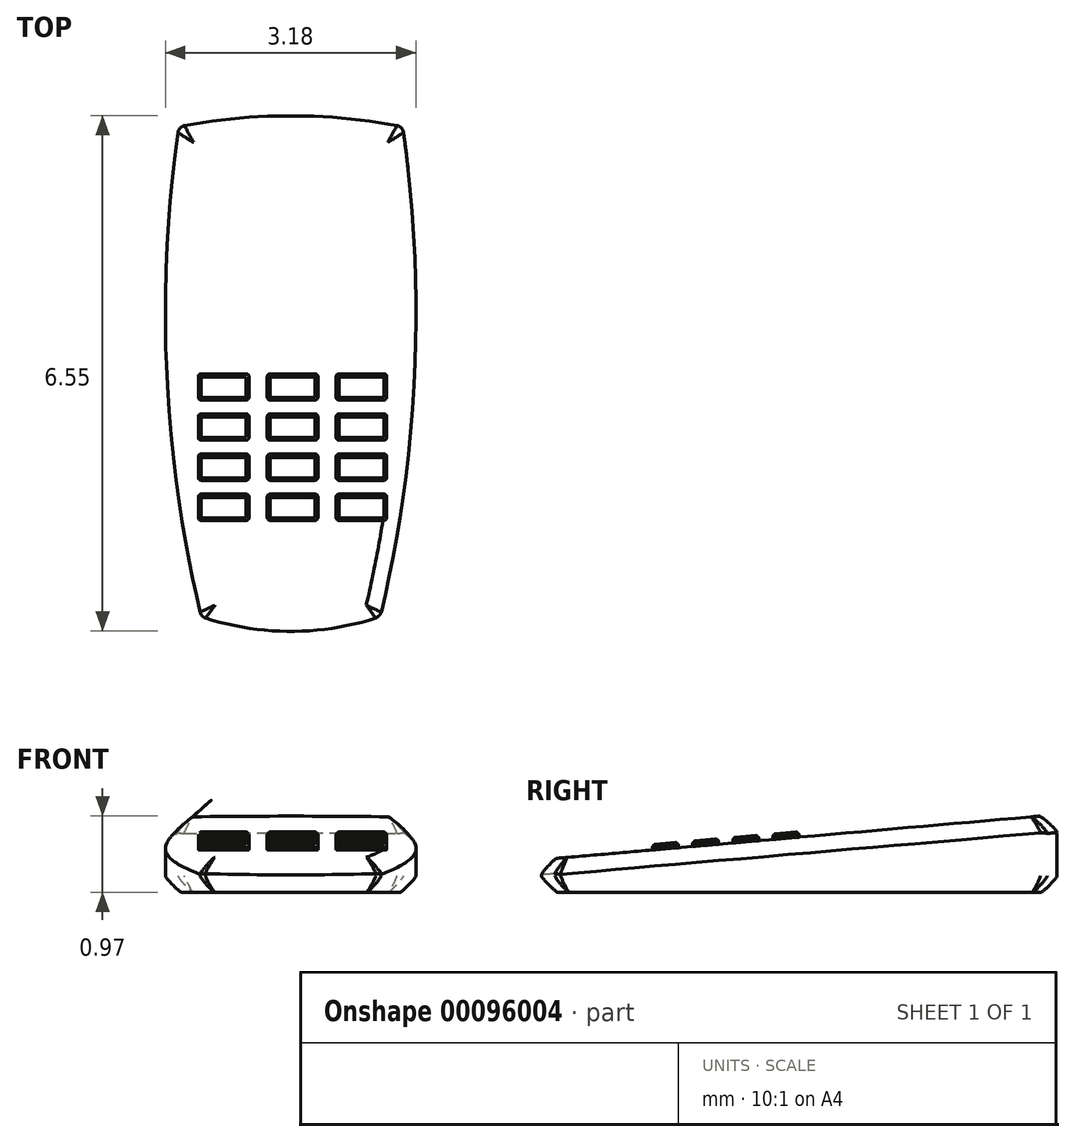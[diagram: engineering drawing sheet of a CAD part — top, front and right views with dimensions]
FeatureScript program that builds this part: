
annotation { "Feature Type Name" : "Feature", "Feature Type Description" : "" }
export const myFeature = defineFeature(function(context is Context, id is Id, definition is map)
    precondition{}
    {
        {
            var Q0;
            Q0=qCreatedBy(makeId("Top.planeOp"),FACE);
            var sketch = newSketch(context, id + "F0", { "sketchPlane" : qUnion([Q0])});
            skPoint(sketch, "E0", {"position": v(-40.64, 114.48) * mm});
            skPoint(sketch, "E1", {"position": v(-32.5, -63.32) * mm});
            skPoint(sketch, "E2.MirrorP", {"position": v(40.64, 114.48) * mm});
            skPoint(sketch, "E3.MirrorP", {"position": v(32.5, -63.32) * mm});
            skArc(sketch, "E4", {"start": v(38.52, 114.88) * mm, "mid": v(0, 118.42) * mm, "end": v(-38.52, 114.88) * mm});
            skArc(sketch, "E5", {"start": v(-40.94, 112.35) * mm, "mid": v(-45, 24.95) * mm, "end": v(-32.89, -61.7) * mm});
            skArc(sketch, "E6", {"start": v(-30.9, -63.86) * mm, "mid": v(0, -68.73) * mm, "end": v(30.9, -63.86) * mm});
            skArc(sketch, "E7.MirrorCS", {"start": v(40.94, 112.35) * mm, "mid": v(45, 24.95) * mm, "end": v(32.89, -61.7) * mm});
            skArc(sketch, "E8.filletArc", {"start": v(-38.52, 114.88) * mm, "mid": v(-40.14, 114) * mm, "end": v(-40.94, 112.35) * mm});
            skArc(sketch, "E9.filletArc", {"start": v(40.94, 112.35) * mm, "mid": v(40.14, 114) * mm, "end": v(38.52, 114.88) * mm});
            skArc(sketch, "E10.filletArc", {"start": v(-32.89, -61.7) * mm, "mid": v(-32.17, -63.04) * mm, "end": v(-30.9, -63.86) * mm});
            skArc(sketch, "E11.filletArc", {"start": v(30.9, -63.86) * mm, "mid": v(32.17, -63.04) * mm, "end": v(32.89, -61.7) * mm});
            skSolve(sketch);
        }
        {
            var Q0;
            Q0=qCreatedBy(makeId("Front.planeOp"),FACE);
            var sketch = newSketch(context, id + "F1", { "sketchPlane" : qUnion([Q0])});
            skLineSegment(sketch, "E12", {"start": v(-58.06, 17.9) * mm, "end": v(59.88, 17.9) * mm, "construction": true});
            skSolve(sketch);
        }
        {
            var Q0;
            Q0=sQuery(id+"F1.wireOp",EDGE,"E12");
            var Q1;
            Q1=qCreatedBy(makeId("Top.planeOp"),FACE);
            cPlane(context, id + "F2", {"entities" : qUnion([Q0, Q1]), "cplaneType" : CPlaneType.LINE_ANGLE, "offset" : 150 * mm, "angle" : 5 * degree, "width" : 150 * mm, "height" : 150 * mm});
        }
        {
            var Q0;
            Q0=makeQuery(id+"F0.imprint","IMPRINT",FACE,{"disambiguationData":[TD([[makeQuery(id+"F0.imprint","IMPRINT",EDGE,{"derivedFrom":sQuery(id+"F0.wireOp",EDGE,"E4")}),1.0]])]});
            var Q1;
            Q1=qCreatedBy(id+"F2.planeOp",FACE);
            extrude(context, id + "F3", {"entities" : qUnion([Q0]), "endBound" : BoundingType.UP_TO_SURFACE, "endBoundEntityFace" : qUnion([Q1]), "depth" : 25 * mm});
        }
        {
            var Q0;
            Q0=makeQuery(id+"F3.opExtrude","CAP_FACE",FACE,{"disambiguationData":[OSD([sQuery(id+"F0.wireOp",EDGE,"E4"),sQuery(id+"F0.wireOp",EDGE,"E5"),sQuery(id+"F0.wireOp",EDGE,"E6"),sQuery(id+"F0.wireOp",EDGE,"E7.MirrorCS"),sQuery(id+"F0.wireOp",EDGE,"E8.filletArc"),sQuery(id+"F0.wireOp",EDGE,"E9.filletArc"),sQuery(id+"F0.wireOp",EDGE,"E10.filletArc"),sQuery(id+"F0.wireOp",EDGE,"E11.filletArc")])],"isStart":false});
            var Q1;
            Q1=makeQuery(id+"F3.opExtrude","CAP_FACE",FACE,{"disambiguationData":[OSD([sQuery(id+"F0.wireOp",EDGE,"E4"),sQuery(id+"F0.wireOp",EDGE,"E5"),sQuery(id+"F0.wireOp",EDGE,"E6"),sQuery(id+"F0.wireOp",EDGE,"E7.MirrorCS"),sQuery(id+"F0.wireOp",EDGE,"E8.filletArc"),sQuery(id+"F0.wireOp",EDGE,"E9.filletArc"),sQuery(id+"F0.wireOp",EDGE,"E10.filletArc"),sQuery(id+"F0.wireOp",EDGE,"E11.filletArc")])],"isStart":true});
            fillet(context, id + "F4", {"entities" : qUnion([Q0, Q1]), "radius" : 6 * mm, "tangentPropagation" : true, "rho" : .1, "crossSection" : FilletCrossSection.CONIC, "allowEdgeOverflow" : false});
        }
        {
            var Q0;
            Q0=makeQuery(id+"F3.opExtrude","CAP_FACE",FACE,{"disambiguationData":[OSD([sQuery(id+"F0.wireOp",EDGE,"E4"),sQuery(id+"F0.wireOp",EDGE,"E5"),sQuery(id+"F0.wireOp",EDGE,"E6"),sQuery(id+"F0.wireOp",EDGE,"E7.MirrorCS"),sQuery(id+"F0.wireOp",EDGE,"E8.filletArc"),sQuery(id+"F0.wireOp",EDGE,"E9.filletArc"),sQuery(id+"F0.wireOp",EDGE,"E10.filletArc"),sQuery(id+"F0.wireOp",EDGE,"E11.filletArc")])],"isStart":false});
            var sketch = newSketch(context, id + "F5", { "sketchPlane" : qUnion([Q0])});
            skLineSegment(sketch, "E13.bottom", {"start": v(-32.5, 16.97) * mm, "end": v(-16.15, 16.97) * mm});
            skLineSegment(sketch, "E13.top", {"start": v(-32.5, 26.44) * mm, "end": v(-16.15, 26.44) * mm});
            skLineSegment(sketch, "E13.left", {"start": v(-33.5, 17.97) * mm, "end": v(-33.5, 25.44) * mm});
            skLineSegment(sketch, "E13.right", {"start": v(-15.15, 17.97) * mm, "end": v(-15.15, 25.44) * mm});
            skPoint(sketch, "E14.visualSharp", {"position": v(-33.5, 26.44) * mm});
            skArc(sketch, "E14.filletArc", {"start": v(-32.5, 26.44) * mm, "mid": v(-33.2, 26.15) * mm, "end": v(-33.5, 25.44) * mm});
            skPoint(sketch, "E15.visualSharp", {"position": v(-15.15, 26.44) * mm});
            skArc(sketch, "E15.filletArc", {"start": v(-15.15, 25.44) * mm, "mid": v(-15.44, 26.15) * mm, "end": v(-16.15, 26.44) * mm});
            skPoint(sketch, "E16.visualSharp", {"position": v(-15.15, 16.97) * mm});
            skArc(sketch, "E16.filletArc", {"start": v(-16.15, 16.97) * mm, "mid": v(-15.44, 17.26) * mm, "end": v(-15.15, 17.97) * mm});
            skPoint(sketch, "E17.visualSharp", {"position": v(-33.5, 16.97) * mm});
            skArc(sketch, "E17.filletArc", {"start": v(-33.5, 17.97) * mm, "mid": v(-33.2, 17.26) * mm, "end": v(-32.5, 16.97) * mm});
            skLineSegment(sketch, "E18.0.1.0", {"start": v(-33.5, 3.35) * mm, "end": v(-33.5, 10.82) * mm});
            skPoint(sketch, "E18.0.1.1", {"position": v(-15.15, 2.35) * mm});
            skLineSegment(sketch, "E18.0.1.2", {"start": v(-15.15, 3.35) * mm, "end": v(-15.15, 10.82) * mm});
            skPoint(sketch, "E18.0.1.3", {"position": v(-33.5, 11.82) * mm});
            skLineSegment(sketch, "E18.0.1.4", {"start": v(-32.5, 2.35) * mm, "end": v(-16.15, 2.35) * mm});
            skPoint(sketch, "E18.0.1.5", {"position": v(-15.15, 11.82) * mm});
            skLineSegment(sketch, "E18.0.1.6", {"start": v(-32.5, 11.82) * mm, "end": v(-16.15, 11.82) * mm});
            skPoint(sketch, "E18.0.1.7", {"position": v(-33.5, 2.35) * mm});
            skArc(sketch, "E18.0.1.8", {"start": v(-33.5, 3.35) * mm, "mid": v(-33.2, 2.65) * mm, "end": v(-32.5, 2.35) * mm});
            skArc(sketch, "E18.0.1.9", {"start": v(-15.15, 10.82) * mm, "mid": v(-15.44, 11.53) * mm, "end": v(-16.15, 11.82) * mm});
            skArc(sketch, "E18.0.1.10", {"start": v(-16.15, 2.35) * mm, "mid": v(-15.44, 2.65) * mm, "end": v(-15.15, 3.35) * mm});
            skArc(sketch, "E18.0.1.11", {"start": v(-32.5, 11.82) * mm, "mid": v(-33.2, 11.53) * mm, "end": v(-33.5, 10.82) * mm});
            skLineSegment(sketch, "E18.0.2.0", {"start": v(-33.5, -11.27) * mm, "end": v(-33.5, -3.8) * mm});
            skPoint(sketch, "E18.0.2.1", {"position": v(-15.15, -12.27) * mm});
            skLineSegment(sketch, "E18.0.2.2", {"start": v(-15.15, -11.27) * mm, "end": v(-15.15, -3.8) * mm});
            skPoint(sketch, "E18.0.2.3", {"position": v(-33.5, -2.8) * mm});
            skLineSegment(sketch, "E18.0.2.4", {"start": v(-32.5, -12.27) * mm, "end": v(-16.15, -12.27) * mm});
            skPoint(sketch, "E18.0.2.5", {"position": v(-15.15, -2.8) * mm});
            skLineSegment(sketch, "E18.0.2.6", {"start": v(-32.5, -2.8) * mm, "end": v(-16.15, -2.8) * mm});
            skPoint(sketch, "E18.0.2.7", {"position": v(-33.5, -12.27) * mm});
            skArc(sketch, "E18.0.2.8", {"start": v(-33.5, -11.27) * mm, "mid": v(-33.2, -11.97) * mm, "end": v(-32.5, -12.27) * mm});
            skArc(sketch, "E18.0.2.9", {"start": v(-15.15, -3.8) * mm, "mid": v(-15.44, -3.09) * mm, "end": v(-16.15, -2.8) * mm});
            skArc(sketch, "E18.0.2.10", {"start": v(-16.15, -12.27) * mm, "mid": v(-15.44, -11.97) * mm, "end": v(-15.15, -11.27) * mm});
            skArc(sketch, "E18.0.2.11", {"start": v(-32.5, -2.8) * mm, "mid": v(-33.2, -3.09) * mm, "end": v(-33.5, -3.8) * mm});
            skLineSegment(sketch, "E18.0.3.0", {"start": v(-33.5, -25.89) * mm, "end": v(-33.5, -18.41) * mm});
            skPoint(sketch, "E18.0.3.1", {"position": v(-15.15, -26.89) * mm});
            skLineSegment(sketch, "E18.0.3.2", {"start": v(-15.15, -25.89) * mm, "end": v(-15.15, -18.41) * mm});
            skPoint(sketch, "E18.0.3.3", {"position": v(-33.5, -17.41) * mm});
            skLineSegment(sketch, "E18.0.3.4", {"start": v(-32.5, -26.89) * mm, "end": v(-16.15, -26.89) * mm});
            skPoint(sketch, "E18.0.3.5", {"position": v(-15.15, -17.41) * mm});
            skLineSegment(sketch, "E18.0.3.6", {"start": v(-32.5, -17.41) * mm, "end": v(-16.15, -17.41) * mm});
            skPoint(sketch, "E18.0.3.7", {"position": v(-33.5, -26.89) * mm});
            skArc(sketch, "E18.0.3.8", {"start": v(-33.5, -25.89) * mm, "mid": v(-33.2, -26.6) * mm, "end": v(-32.5, -26.89) * mm});
            skArc(sketch, "E18.0.3.9", {"start": v(-15.15, -18.41) * mm, "mid": v(-15.44, -17.7) * mm, "end": v(-16.15, -17.41) * mm});
            skArc(sketch, "E18.0.3.10", {"start": v(-16.15, -26.89) * mm, "mid": v(-15.44, -26.6) * mm, "end": v(-15.15, -25.89) * mm});
            skArc(sketch, "E18.0.3.11", {"start": v(-32.5, -17.41) * mm, "mid": v(-33.2, -17.7) * mm, "end": v(-33.5, -18.41) * mm});
            skLineSegment(sketch, "E18.1.0.0", {"start": v(-8.5, 17.97) * mm, "end": v(-8.5, 25.44) * mm});
            skPoint(sketch, "E18.1.0.1", {"position": v(9.85, 16.97) * mm});
            skLineSegment(sketch, "E18.1.0.2", {"start": v(9.85, 17.97) * mm, "end": v(9.85, 25.44) * mm});
            skPoint(sketch, "E18.1.0.3", {"position": v(-8.5, 26.44) * mm});
            skLineSegment(sketch, "E18.1.0.4", {"start": v(-7.5, 16.97) * mm, "end": v(8.85, 16.97) * mm});
            skPoint(sketch, "E18.1.0.5", {"position": v(9.85, 26.44) * mm});
            skLineSegment(sketch, "E18.1.0.6", {"start": v(-7.5, 26.44) * mm, "end": v(8.85, 26.44) * mm});
            skPoint(sketch, "E18.1.0.7", {"position": v(-8.5, 16.97) * mm});
            skArc(sketch, "E18.1.0.8", {"start": v(-8.5, 17.97) * mm, "mid": v(-8.2, 17.26) * mm, "end": v(-7.5, 16.97) * mm});
            skArc(sketch, "E18.1.0.9", {"start": v(9.85, 25.44) * mm, "mid": v(9.56, 26.15) * mm, "end": v(8.85, 26.44) * mm});
            skArc(sketch, "E18.1.0.10", {"start": v(8.85, 16.97) * mm, "mid": v(9.56, 17.26) * mm, "end": v(9.85, 17.97) * mm});
            skArc(sketch, "E18.1.0.11", {"start": v(-7.5, 26.44) * mm, "mid": v(-8.2, 26.15) * mm, "end": v(-8.5, 25.44) * mm});
            skLineSegment(sketch, "E18.1.1.0", {"start": v(-8.5, 3.35) * mm, "end": v(-8.5, 10.82) * mm});
            skPoint(sketch, "E18.1.1.1", {"position": v(9.85, 2.35) * mm});
            skLineSegment(sketch, "E18.1.1.2", {"start": v(9.85, 3.35) * mm, "end": v(9.85, 10.82) * mm});
            skPoint(sketch, "E18.1.1.3", {"position": v(-8.5, 11.82) * mm});
            skLineSegment(sketch, "E18.1.1.4", {"start": v(-7.5, 2.35) * mm, "end": v(8.85, 2.35) * mm});
            skPoint(sketch, "E18.1.1.5", {"position": v(9.85, 11.82) * mm});
            skLineSegment(sketch, "E18.1.1.6", {"start": v(-7.5, 11.82) * mm, "end": v(8.85, 11.82) * mm});
            skPoint(sketch, "E18.1.1.7", {"position": v(-8.5, 2.35) * mm});
            skArc(sketch, "E18.1.1.8", {"start": v(-8.5, 3.35) * mm, "mid": v(-8.2, 2.65) * mm, "end": v(-7.5, 2.35) * mm});
            skArc(sketch, "E18.1.1.9", {"start": v(9.85, 10.82) * mm, "mid": v(9.56, 11.53) * mm, "end": v(8.85, 11.82) * mm});
            skArc(sketch, "E18.1.1.10", {"start": v(8.85, 2.35) * mm, "mid": v(9.56, 2.65) * mm, "end": v(9.85, 3.35) * mm});
            skArc(sketch, "E18.1.1.11", {"start": v(-7.5, 11.82) * mm, "mid": v(-8.2, 11.53) * mm, "end": v(-8.5, 10.82) * mm});
            skLineSegment(sketch, "E18.1.2.0", {"start": v(-8.5, -11.27) * mm, "end": v(-8.5, -3.8) * mm});
            skPoint(sketch, "E18.1.2.1", {"position": v(9.85, -12.27) * mm});
            skLineSegment(sketch, "E18.1.2.2", {"start": v(9.85, -11.27) * mm, "end": v(9.85, -3.8) * mm});
            skPoint(sketch, "E18.1.2.3", {"position": v(-8.5, -2.8) * mm});
            skLineSegment(sketch, "E18.1.2.4", {"start": v(-7.5, -12.27) * mm, "end": v(8.85, -12.27) * mm});
            skPoint(sketch, "E18.1.2.5", {"position": v(9.85, -2.8) * mm});
            skLineSegment(sketch, "E18.1.2.6", {"start": v(-7.5, -2.8) * mm, "end": v(8.85, -2.8) * mm});
            skPoint(sketch, "E18.1.2.7", {"position": v(-8.5, -12.27) * mm});
            skArc(sketch, "E18.1.2.8", {"start": v(-8.5, -11.27) * mm, "mid": v(-8.2, -11.97) * mm, "end": v(-7.5, -12.27) * mm});
            skArc(sketch, "E18.1.2.9", {"start": v(9.85, -3.8) * mm, "mid": v(9.56, -3.09) * mm, "end": v(8.85, -2.8) * mm});
            skArc(sketch, "E18.1.2.10", {"start": v(8.85, -12.27) * mm, "mid": v(9.56, -11.97) * mm, "end": v(9.85, -11.27) * mm});
            skArc(sketch, "E18.1.2.11", {"start": v(-7.5, -2.8) * mm, "mid": v(-8.2, -3.09) * mm, "end": v(-8.5, -3.8) * mm});
            skLineSegment(sketch, "E18.1.3.0", {"start": v(-8.5, -25.89) * mm, "end": v(-8.5, -18.41) * mm});
            skPoint(sketch, "E18.1.3.1", {"position": v(9.85, -26.89) * mm});
            skLineSegment(sketch, "E18.1.3.2", {"start": v(9.85, -25.89) * mm, "end": v(9.85, -18.41) * mm});
            skPoint(sketch, "E18.1.3.3", {"position": v(-8.5, -17.41) * mm});
            skLineSegment(sketch, "E18.1.3.4", {"start": v(-7.5, -26.89) * mm, "end": v(8.85, -26.89) * mm});
            skPoint(sketch, "E18.1.3.5", {"position": v(9.85, -17.41) * mm});
            skLineSegment(sketch, "E18.1.3.6", {"start": v(-7.5, -17.41) * mm, "end": v(8.85, -17.41) * mm});
            skPoint(sketch, "E18.1.3.7", {"position": v(-8.5, -26.89) * mm});
            skArc(sketch, "E18.1.3.8", {"start": v(-8.5, -25.89) * mm, "mid": v(-8.2, -26.6) * mm, "end": v(-7.5, -26.89) * mm});
            skArc(sketch, "E18.1.3.9", {"start": v(9.85, -18.41) * mm, "mid": v(9.56, -17.7) * mm, "end": v(8.85, -17.41) * mm});
            skArc(sketch, "E18.1.3.10", {"start": v(8.85, -26.89) * mm, "mid": v(9.56, -26.6) * mm, "end": v(9.85, -25.89) * mm});
            skArc(sketch, "E18.1.3.11", {"start": v(-7.5, -17.41) * mm, "mid": v(-8.2, -17.7) * mm, "end": v(-8.5, -18.41) * mm});
            skLineSegment(sketch, "E18.2.0.0", {"start": v(16.5, 17.97) * mm, "end": v(16.5, 25.44) * mm});
            skPoint(sketch, "E18.2.0.1", {"position": v(34.85, 16.97) * mm});
            skLineSegment(sketch, "E18.2.0.2", {"start": v(34.85, 17.97) * mm, "end": v(34.85, 25.44) * mm});
            skPoint(sketch, "E18.2.0.3", {"position": v(16.5, 26.44) * mm});
            skLineSegment(sketch, "E18.2.0.4", {"start": v(17.5, 16.97) * mm, "end": v(33.85, 16.97) * mm});
            skPoint(sketch, "E18.2.0.5", {"position": v(34.85, 26.44) * mm});
            skLineSegment(sketch, "E18.2.0.6", {"start": v(17.5, 26.44) * mm, "end": v(33.85, 26.44) * mm});
            skPoint(sketch, "E18.2.0.7", {"position": v(16.5, 16.97) * mm});
            skArc(sketch, "E18.2.0.8", {"start": v(16.5, 17.97) * mm, "mid": v(16.8, 17.26) * mm, "end": v(17.5, 16.97) * mm});
            skArc(sketch, "E18.2.0.9", {"start": v(34.85, 25.44) * mm, "mid": v(34.56, 26.15) * mm, "end": v(33.85, 26.44) * mm});
            skArc(sketch, "E18.2.0.10", {"start": v(33.85, 16.97) * mm, "mid": v(34.56, 17.26) * mm, "end": v(34.85, 17.97) * mm});
            skArc(sketch, "E18.2.0.11", {"start": v(17.5, 26.44) * mm, "mid": v(16.8, 26.15) * mm, "end": v(16.5, 25.44) * mm});
            skLineSegment(sketch, "E18.2.1.0", {"start": v(16.5, 3.35) * mm, "end": v(16.5, 10.82) * mm});
            skPoint(sketch, "E18.2.1.1", {"position": v(34.85, 2.35) * mm});
            skLineSegment(sketch, "E18.2.1.2", {"start": v(34.85, 3.35) * mm, "end": v(34.85, 10.82) * mm});
            skPoint(sketch, "E18.2.1.3", {"position": v(16.5, 11.82) * mm});
            skLineSegment(sketch, "E18.2.1.4", {"start": v(17.5, 2.35) * mm, "end": v(33.85, 2.35) * mm});
            skPoint(sketch, "E18.2.1.5", {"position": v(34.85, 11.82) * mm});
            skLineSegment(sketch, "E18.2.1.6", {"start": v(17.5, 11.82) * mm, "end": v(33.85, 11.82) * mm});
            skPoint(sketch, "E18.2.1.7", {"position": v(16.5, 2.35) * mm});
            skArc(sketch, "E18.2.1.8", {"start": v(16.5, 3.35) * mm, "mid": v(16.8, 2.65) * mm, "end": v(17.5, 2.35) * mm});
            skArc(sketch, "E18.2.1.9", {"start": v(34.85, 10.82) * mm, "mid": v(34.56, 11.53) * mm, "end": v(33.85, 11.82) * mm});
            skArc(sketch, "E18.2.1.10", {"start": v(33.85, 2.35) * mm, "mid": v(34.56, 2.65) * mm, "end": v(34.85, 3.35) * mm});
            skArc(sketch, "E18.2.1.11", {"start": v(17.5, 11.82) * mm, "mid": v(16.8, 11.53) * mm, "end": v(16.5, 10.82) * mm});
            skLineSegment(sketch, "E18.2.2.0", {"start": v(16.5, -11.27) * mm, "end": v(16.5, -3.8) * mm});
            skPoint(sketch, "E18.2.2.1", {"position": v(34.85, -12.27) * mm});
            skLineSegment(sketch, "E18.2.2.2", {"start": v(34.85, -11.27) * mm, "end": v(34.85, -3.8) * mm});
            skPoint(sketch, "E18.2.2.3", {"position": v(16.5, -2.8) * mm});
            skLineSegment(sketch, "E18.2.2.4", {"start": v(17.5, -12.27) * mm, "end": v(33.85, -12.27) * mm});
            skPoint(sketch, "E18.2.2.5", {"position": v(34.85, -2.8) * mm});
            skLineSegment(sketch, "E18.2.2.6", {"start": v(17.5, -2.8) * mm, "end": v(33.85, -2.8) * mm});
            skPoint(sketch, "E18.2.2.7", {"position": v(16.5, -12.27) * mm});
            skArc(sketch, "E18.2.2.8", {"start": v(16.5, -11.27) * mm, "mid": v(16.8, -11.97) * mm, "end": v(17.5, -12.27) * mm});
            skArc(sketch, "E18.2.2.9", {"start": v(34.85, -3.8) * mm, "mid": v(34.56, -3.09) * mm, "end": v(33.85, -2.8) * mm});
            skArc(sketch, "E18.2.2.10", {"start": v(33.85, -12.27) * mm, "mid": v(34.56, -11.97) * mm, "end": v(34.85, -11.27) * mm});
            skArc(sketch, "E18.2.2.11", {"start": v(17.5, -2.8) * mm, "mid": v(16.8, -3.09) * mm, "end": v(16.5, -3.8) * mm});
            skLineSegment(sketch, "E18.2.3.0", {"start": v(16.5, -25.89) * mm, "end": v(16.5, -18.41) * mm});
            skPoint(sketch, "E18.2.3.1", {"position": v(34.85, -26.89) * mm});
            skLineSegment(sketch, "E18.2.3.2", {"start": v(34.85, -25.89) * mm, "end": v(34.85, -18.41) * mm});
            skPoint(sketch, "E18.2.3.3", {"position": v(16.5, -17.41) * mm});
            skLineSegment(sketch, "E18.2.3.4", {"start": v(17.5, -26.89) * mm, "end": v(33.85, -26.89) * mm});
            skPoint(sketch, "E18.2.3.5", {"position": v(34.85, -17.41) * mm});
            skLineSegment(sketch, "E18.2.3.6", {"start": v(17.5, -17.41) * mm, "end": v(33.85, -17.41) * mm});
            skPoint(sketch, "E18.2.3.7", {"position": v(16.5, -26.89) * mm});
            skArc(sketch, "E18.2.3.8", {"start": v(16.5, -25.89) * mm, "mid": v(16.8, -26.6) * mm, "end": v(17.5, -26.89) * mm});
            skArc(sketch, "E18.2.3.9", {"start": v(34.85, -18.41) * mm, "mid": v(34.56, -17.7) * mm, "end": v(33.85, -17.41) * mm});
            skArc(sketch, "E18.2.3.10", {"start": v(33.85, -26.89) * mm, "mid": v(34.56, -26.6) * mm, "end": v(34.85, -25.89) * mm});
            skArc(sketch, "E18.2.3.11", {"start": v(17.5, -17.41) * mm, "mid": v(16.8, -17.7) * mm, "end": v(16.5, -18.41) * mm});
            skLineSegment(sketch, "E18.direction1", {"start": v(-33.5, 17.97) * mm, "end": v(-8.5, 17.97) * mm, "construction": true});
            skLineSegment(sketch, "E18.direction2", {"start": v(-33.5, 17.97) * mm, "end": v(-33.5, 3.35) * mm, "construction": true});
            skSolve(sketch);
        }
        {
            var Q0;
            Q0 = qSketchRegion(id + "F5", true);
            extrude(context, id + "F6", {"entities" : qUnion([Q0]), "operationType" : NewBodyOperationType.ADD, "depth" : 2 * mm});
        }
        {
            var Q0;
            Q0=makeQuery(id+"F6.opExtrude","CAP_FACE",FACE,{"disambiguationData":[OSD([sQuery(id+"F5.wireOp",EDGE,"E13.bottom"),sQuery(id+"F5.wireOp",EDGE,"E13.top"),sQuery(id+"F5.wireOp",EDGE,"E13.left"),sQuery(id+"F5.wireOp",EDGE,"E13.right"),sQuery(id+"F5.wireOp",EDGE,"E14.filletArc"),sQuery(id+"F5.wireOp",EDGE,"E15.filletArc"),sQuery(id+"F5.wireOp",EDGE,"E16.filletArc"),sQuery(id+"F5.wireOp",EDGE,"E17.filletArc")])],"isStart":false});
            var Q1;
            Q1=makeQuery(id+"F6.opExtrude","CAP_FACE",FACE,{"disambiguationData":[OSD([sQuery(id+"F5.wireOp",EDGE,"E18.1.0.0"),sQuery(id+"F5.wireOp",EDGE,"E18.1.0.2"),sQuery(id+"F5.wireOp",EDGE,"E18.1.0.4"),sQuery(id+"F5.wireOp",EDGE,"E18.1.0.6"),sQuery(id+"F5.wireOp",EDGE,"E18.1.0.8"),sQuery(id+"F5.wireOp",EDGE,"E18.1.0.9"),sQuery(id+"F5.wireOp",EDGE,"E18.1.0.10"),sQuery(id+"F5.wireOp",EDGE,"E18.1.0.11")])],"isStart":false});
            var Q2;
            Q2=makeQuery(id+"F6.opExtrude","CAP_FACE",FACE,{"disambiguationData":[OSD([sQuery(id+"F5.wireOp",EDGE,"E18.2.0.0"),sQuery(id+"F5.wireOp",EDGE,"E18.2.0.2"),sQuery(id+"F5.wireOp",EDGE,"E18.2.0.4"),sQuery(id+"F5.wireOp",EDGE,"E18.2.0.6"),sQuery(id+"F5.wireOp",EDGE,"E18.2.0.8"),sQuery(id+"F5.wireOp",EDGE,"E18.2.0.9"),sQuery(id+"F5.wireOp",EDGE,"E18.2.0.10"),sQuery(id+"F5.wireOp",EDGE,"E18.2.0.11")])],"isStart":false});
            var Q3;
            Q3=makeQuery(id+"F6.opExtrude","CAP_FACE",FACE,{"disambiguationData":[OSD([sQuery(id+"F5.wireOp",EDGE,"E18.2.1.0"),sQuery(id+"F5.wireOp",EDGE,"E18.2.1.2"),sQuery(id+"F5.wireOp",EDGE,"E18.2.1.4"),sQuery(id+"F5.wireOp",EDGE,"E18.2.1.6"),sQuery(id+"F5.wireOp",EDGE,"E18.2.1.8"),sQuery(id+"F5.wireOp",EDGE,"E18.2.1.9"),sQuery(id+"F5.wireOp",EDGE,"E18.2.1.10"),sQuery(id+"F5.wireOp",EDGE,"E18.2.1.11")])],"isStart":false});
            var Q4;
            Q4=makeQuery(id+"F6.opExtrude","CAP_FACE",FACE,{"disambiguationData":[OSD([sQuery(id+"F5.wireOp",EDGE,"E18.1.1.0"),sQuery(id+"F5.wireOp",EDGE,"E18.1.1.2"),sQuery(id+"F5.wireOp",EDGE,"E18.1.1.4"),sQuery(id+"F5.wireOp",EDGE,"E18.1.1.6"),sQuery(id+"F5.wireOp",EDGE,"E18.1.1.8"),sQuery(id+"F5.wireOp",EDGE,"E18.1.1.9"),sQuery(id+"F5.wireOp",EDGE,"E18.1.1.10"),sQuery(id+"F5.wireOp",EDGE,"E18.1.1.11")])],"isStart":false});
            var Q5;
            Q5=makeQuery(id+"F6.opExtrude","CAP_FACE",FACE,{"disambiguationData":[OSD([sQuery(id+"F5.wireOp",EDGE,"E18.0.1.0"),sQuery(id+"F5.wireOp",EDGE,"E18.0.1.2"),sQuery(id+"F5.wireOp",EDGE,"E18.0.1.4"),sQuery(id+"F5.wireOp",EDGE,"E18.0.1.6"),sQuery(id+"F5.wireOp",EDGE,"E18.0.1.8"),sQuery(id+"F5.wireOp",EDGE,"E18.0.1.9"),sQuery(id+"F5.wireOp",EDGE,"E18.0.1.10"),sQuery(id+"F5.wireOp",EDGE,"E18.0.1.11")])],"isStart":false});
            var Q6;
            Q6=makeQuery(id+"F6.opExtrude","CAP_FACE",FACE,{"disambiguationData":[OSD([sQuery(id+"F5.wireOp",EDGE,"E18.0.2.0"),sQuery(id+"F5.wireOp",EDGE,"E18.0.2.2"),sQuery(id+"F5.wireOp",EDGE,"E18.0.2.4"),sQuery(id+"F5.wireOp",EDGE,"E18.0.2.6"),sQuery(id+"F5.wireOp",EDGE,"E18.0.2.8"),sQuery(id+"F5.wireOp",EDGE,"E18.0.2.9"),sQuery(id+"F5.wireOp",EDGE,"E18.0.2.10"),sQuery(id+"F5.wireOp",EDGE,"E18.0.2.11")])],"isStart":false});
            var Q7;
            Q7=makeQuery(id+"F6.opExtrude","CAP_FACE",FACE,{"disambiguationData":[OSD([sQuery(id+"F5.wireOp",EDGE,"E18.1.2.0"),sQuery(id+"F5.wireOp",EDGE,"E18.1.2.2"),sQuery(id+"F5.wireOp",EDGE,"E18.1.2.4"),sQuery(id+"F5.wireOp",EDGE,"E18.1.2.6"),sQuery(id+"F5.wireOp",EDGE,"E18.1.2.8"),sQuery(id+"F5.wireOp",EDGE,"E18.1.2.9"),sQuery(id+"F5.wireOp",EDGE,"E18.1.2.10"),sQuery(id+"F5.wireOp",EDGE,"E18.1.2.11")])],"isStart":false});
            var Q8;
            Q8=makeQuery(id+"F6.opExtrude","CAP_FACE",FACE,{"disambiguationData":[OSD([sQuery(id+"F5.wireOp",EDGE,"E18.2.2.0"),sQuery(id+"F5.wireOp",EDGE,"E18.2.2.2"),sQuery(id+"F5.wireOp",EDGE,"E18.2.2.4"),sQuery(id+"F5.wireOp",EDGE,"E18.2.2.6"),sQuery(id+"F5.wireOp",EDGE,"E18.2.2.8"),sQuery(id+"F5.wireOp",EDGE,"E18.2.2.9"),sQuery(id+"F5.wireOp",EDGE,"E18.2.2.10"),sQuery(id+"F5.wireOp",EDGE,"E18.2.2.11")])],"isStart":false});
            var Q9;
            Q9=makeQuery(id+"F6.opExtrude","CAP_FACE",FACE,{"disambiguationData":[OSD([sQuery(id+"F5.wireOp",EDGE,"E18.2.3.0"),sQuery(id+"F5.wireOp",EDGE,"E18.2.3.2"),sQuery(id+"F5.wireOp",EDGE,"E18.2.3.4"),sQuery(id+"F5.wireOp",EDGE,"E18.2.3.6"),sQuery(id+"F5.wireOp",EDGE,"E18.2.3.8"),sQuery(id+"F5.wireOp",EDGE,"E18.2.3.9"),sQuery(id+"F5.wireOp",EDGE,"E18.2.3.10"),sQuery(id+"F5.wireOp",EDGE,"E18.2.3.11")])],"isStart":false});
            var Q10;
            Q10=makeQuery(id+"F6.opExtrude","CAP_FACE",FACE,{"disambiguationData":[OSD([sQuery(id+"F5.wireOp",EDGE,"E18.1.3.0"),sQuery(id+"F5.wireOp",EDGE,"E18.1.3.2"),sQuery(id+"F5.wireOp",EDGE,"E18.1.3.4"),sQuery(id+"F5.wireOp",EDGE,"E18.1.3.6"),sQuery(id+"F5.wireOp",EDGE,"E18.1.3.8"),sQuery(id+"F5.wireOp",EDGE,"E18.1.3.9"),sQuery(id+"F5.wireOp",EDGE,"E18.1.3.10"),sQuery(id+"F5.wireOp",EDGE,"E18.1.3.11")])],"isStart":false});
            var Q11;
            Q11=makeQuery(id+"F6.opExtrude","CAP_FACE",FACE,{"disambiguationData":[OSD([sQuery(id+"F5.wireOp",EDGE,"E18.0.3.0"),sQuery(id+"F5.wireOp",EDGE,"E18.0.3.2"),sQuery(id+"F5.wireOp",EDGE,"E18.0.3.4"),sQuery(id+"F5.wireOp",EDGE,"E18.0.3.6"),sQuery(id+"F5.wireOp",EDGE,"E18.0.3.8"),sQuery(id+"F5.wireOp",EDGE,"E18.0.3.9"),sQuery(id+"F5.wireOp",EDGE,"E18.0.3.10"),sQuery(id+"F5.wireOp",EDGE,"E18.0.3.11")])],"isStart":false});
            fillet(context, id + "F7", {"entities" : qUnion([Q0, Q1, Q2, Q3, Q4, Q5, Q6, Q7, Q8, Q9, Q10, Q11]), "radius" : 1 * mm, "tangentPropagation" : true, "rho" : .2, "crossSection" : FilletCrossSection.CONIC, "allowEdgeOverflow" : false});
        }
        {
            var Q0;
            Q0=makeQuery(id+"F3.opExtrude","CAP_FACE",FACE,{"disambiguationData":[OSD([sQuery(id+"F0.wireOp",EDGE,"E4"),sQuery(id+"F0.wireOp",EDGE,"E5"),sQuery(id+"F0.wireOp",EDGE,"E6"),sQuery(id+"F0.wireOp",EDGE,"E7.MirrorCS"),sQuery(id+"F0.wireOp",EDGE,"E8.filletArc"),sQuery(id+"F0.wireOp",EDGE,"E9.filletArc"),sQuery(id+"F0.wireOp",EDGE,"E10.filletArc"),sQuery(id+"F0.wireOp",EDGE,"E11.filletArc")])],"isStart":true});
            var sketch = newSketch(context, id + "F8", { "sketchPlane" : qUnion([Q0])});
            skPoint(sketch, "E19", {"position": v(0, -31.44) * mm});
            skSolve(sketch);
        }
        {
            var Q0;
            Q0=makeQuery(id+"F3.opExtrude","SWEPT_BODY",BODY,{"disambiguationData":[OSD([sQuery(id+"F0.wireOp",EDGE,"E4"),sQuery(id+"F0.wireOp",EDGE,"E5"),sQuery(id+"F0.wireOp",EDGE,"E6"),sQuery(id+"F0.wireOp",EDGE,"E7.MirrorCS"),sQuery(id+"F0.wireOp",EDGE,"E8.filletArc"),sQuery(id+"F0.wireOp",EDGE,"E9.filletArc"),sQuery(id+"F0.wireOp",EDGE,"E10.filletArc"),sQuery(id+"F0.wireOp",EDGE,"E11.filletArc")])]});
            var Q1;
            Q1=sQuery(id+"F8.wireOp",VERTEX,"E19");
            transform(context, id + "F9", {"entities" : qUnion([Q0]), "transformType" : TransformType.SCALE_UNIFORMLY, "scale" : 0.04, "scalePoint" : qUnion([Q1]), "makeCopy" : false});
        }
    });
